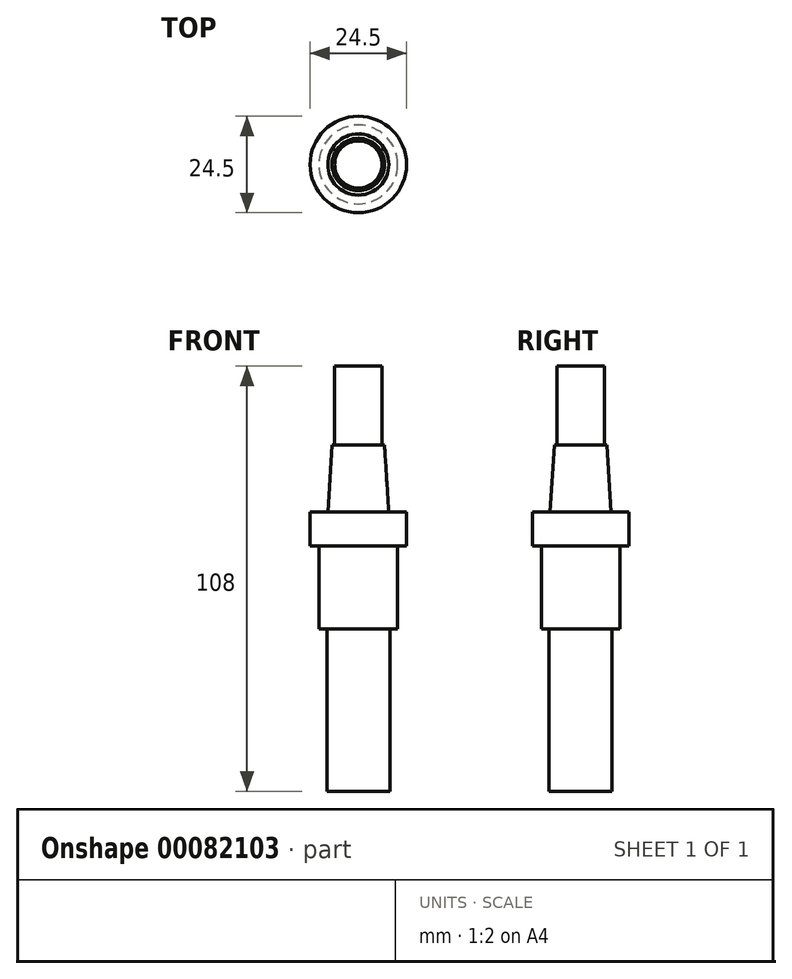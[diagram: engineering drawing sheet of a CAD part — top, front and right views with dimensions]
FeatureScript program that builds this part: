
annotation { "Feature Type Name" : "Feature", "Feature Type Description" : "" }
export const myFeature = defineFeature(function(context is Context, id is Id, definition is map)
    precondition{}
    {
        {
            var Q0;
            Q0=qCreatedBy(makeId("Front.planeOp"),FACE);
            var sketch = newSketch(context, id + "F0", { "sketchPlane" : qUnion([Q0])});
            skLineSegment(sketch, "E0", {"start": v(0, 0) * mm, "end": v(6, 0) * mm});
            skLineSegment(sketch, "E1", {"start": v(6, 0) * mm, "end": v(6, -20) * mm});
            skLineSegment(sketch, "E2", {"start": v(6, -20) * mm, "end": v(6.65, -20) * mm});
            skLineSegment(sketch, "E3", {"start": v(6.65, -20) * mm, "end": v(7.75, -37) * mm});
            skLineSegment(sketch, "E4", {"start": v(7.75, -37) * mm, "end": v(12.25, -37) * mm});
            skLineSegment(sketch, "E5", {"start": v(12.25, -37) * mm, "end": v(12.25, -45.7) * mm});
            skLineSegment(sketch, "E6", {"start": v(12.25, -45.7) * mm, "end": v(10, -45.7) * mm});
            skLineSegment(sketch, "E7", {"start": v(10, -45.7) * mm, "end": v(10, -66.7) * mm});
            skLineSegment(sketch, "E8", {"start": v(10, -66.7) * mm, "end": v(8, -66.7) * mm});
            skLineSegment(sketch, "E9", {"start": v(8, -66.7) * mm, "end": v(8, -108) * mm});
            skLineSegment(sketch, "E10", {"start": v(8, -108) * mm, "end": v(0, -108) * mm});
            skLineSegment(sketch, "E11", {"start": v(0, 0) * mm, "end": v(0, -108) * mm});
            skSolve(sketch);
        }
        {
            var Q0;
            Q0 = qSketchRegion(id + "F0", true);
            var Q1;
            Q1=sQuery(id+"F0.wireOp",EDGE,"E11");
            revolve(context, id + "F1", {"entities" : qUnion([Q0]), "axis" : qUnion([Q1]), "revolveType" : RevolveType.FULL});
        }
    });
